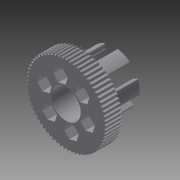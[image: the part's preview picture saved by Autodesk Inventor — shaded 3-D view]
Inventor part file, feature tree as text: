
AUTODESK INVENTOR PART (.ipt)
format: ipt  version: 2015 SP1 (Build 190203100, 203)  size: 923,136 bytes
history: native  units: in
note: dims shown in document units (in); Inventor stores cm internally (conversion verified against a paired STEP export)
features: reference x14, other x5, extrude x4, sketch x3, chamfer x2, hole x1, fillet x1, pattern_circular x1
ambient origin geometry x8: Origin, YZ Plane, XZ Plane, XY Plane, X Axis, Y Axis, Z Axis, Center Point
bodies: Solid1 (feature_tree), Solid2 (feature_tree)
feature tree (31):
  other  "PrintablePulley HTD3mm 66T"
  extrude  "Spacer"  Depth=0.22in TaperAngle=45.0deg
  extrude  "Center Hole"  Depth=0.75in TaperAngle=0.0deg
  chamfer  "Spacer Chamfer"  Distance=0.395in
  extrude  "Spoke"  Depth=0.3937in
  other  "InsideFaceOfGear"
  other  "Nut Pocket Sketch"
  hole  "No8 Clearance"  [1 undecoded]
  extrude  "Nut Pocket"  Depth=0.3937in
  fillet  "Fillet7"  Radius=0.505in
  chamfer  "Spoke Chamfer3"  Distance=0.045in Angle=45.0deg
  pattern_circular  "Circular Pattern4"  Count=6 Angle=360.0deg
  sketch  "Sketch2"  dims[d2=0.22in d3=0.0in d4=0.22in d5=0.22in d6=45.0deg]
  sketch  "Sketch5"  dims[d12=0.58in d13=0.0in d35=0.75in d36=0.0in]
  sketch  "Sketch9"  dims[d37=1.0in d38=1.0in d39=0.225in d40=0.75in d41=0.375in d42=0.25in d43=0.5635in d44=1.0in d45=0.8108in d46=0.395in d65=0.02in d71=0.155in d74=0.3937in d75=0.505in d77=0.045in d78=0.045in d79=45.0deg d80=2.3622in d81=360.0deg d84=0.0in]
  reference  "Reference40"
  reference  "Reference41"
  reference  "Reference42"
  reference  "Reference43"
  reference  "Reference44"
  reference  "Reference45"
  reference  "Reference46"
  reference  "Reference47"
  reference  "Reference48"
  reference  "Reference49"
  reference  "Reference50"
  reference  "Reference51"
  reference  "Reference52"
  reference  "Reference53"
  other  "Solid1::PrintablePulley HTD3mm 66T"
  other  "TaggingFeature1"
note: 1 required parameter value undecoded (feature->parameter linkage not recoverable at this tier; creation-order binding heuristic only, values carry confidence <= 0.55)
